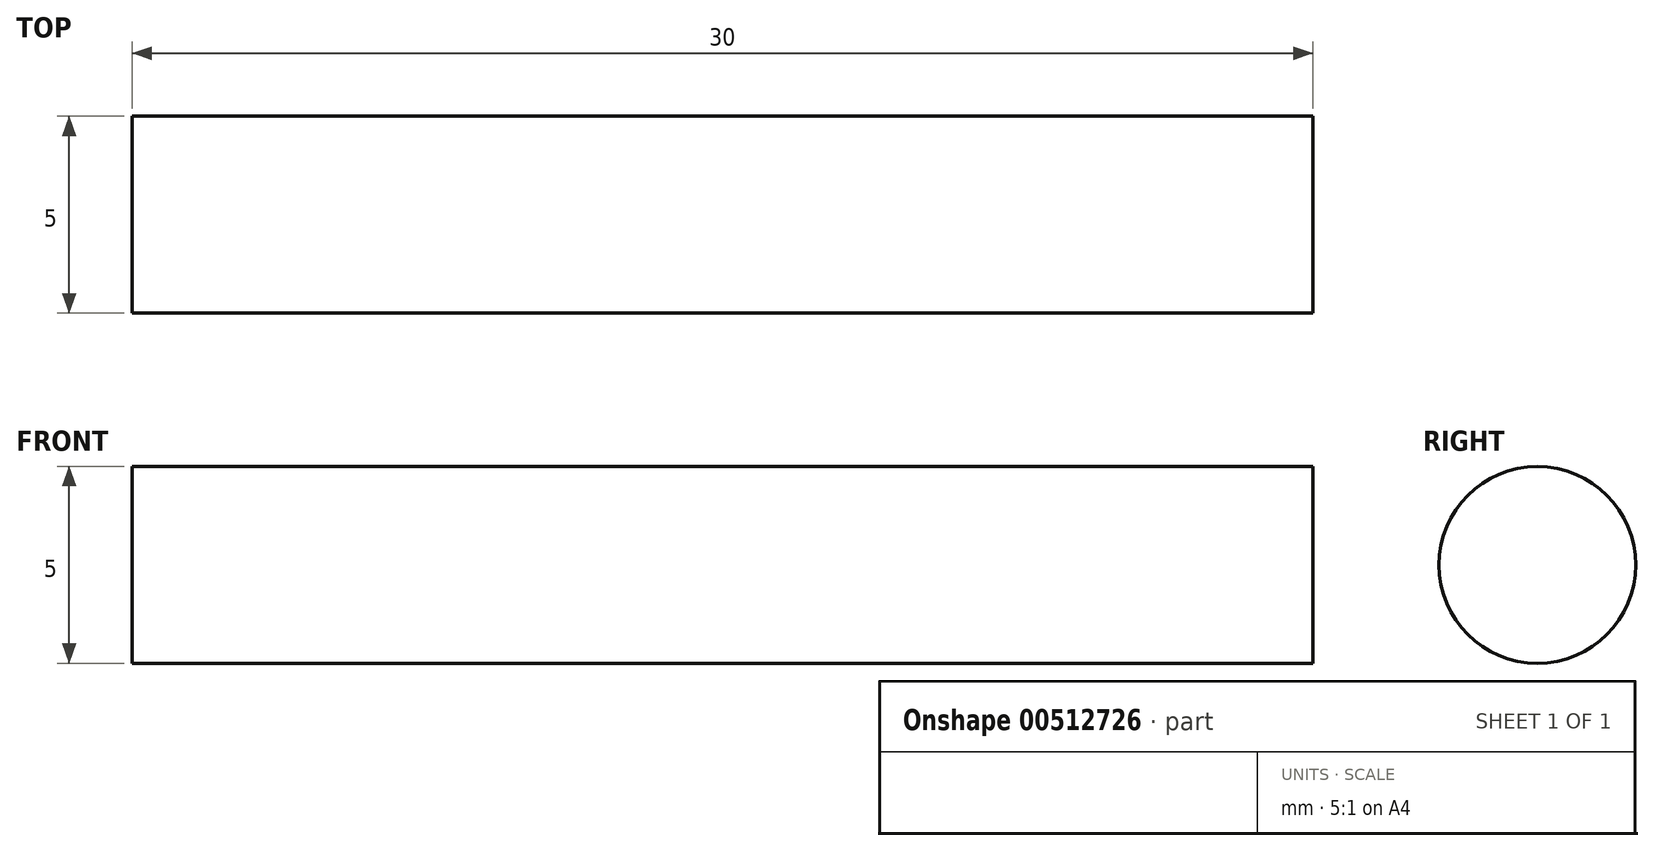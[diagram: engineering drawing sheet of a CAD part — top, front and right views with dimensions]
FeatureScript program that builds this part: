
annotation { "Feature Type Name" : "Feature", "Feature Type Description" : "" }
export const myFeature = defineFeature(function(context is Context, id is Id, definition is map)
    precondition{}
    {
        {
            var Q0;
            Q0=qCreatedBy(makeId("Right.planeOp"),FACE);
            var sketch = newSketch(context, id + "F0", { "sketchPlane" : qUnion([Q0])});
            skCircle(sketch, "E0", {"center": v(0, 0) * mm, "radius": 2.5 * mm});
            skSolve(sketch);
        }
        {
            var Q0;
            Q0 = qSketchRegion(id + "F0", true);
            extrude(context, id + "F1", {"entities" : qUnion([Q0]), "depth" : 30 * mm});
        }
    });
